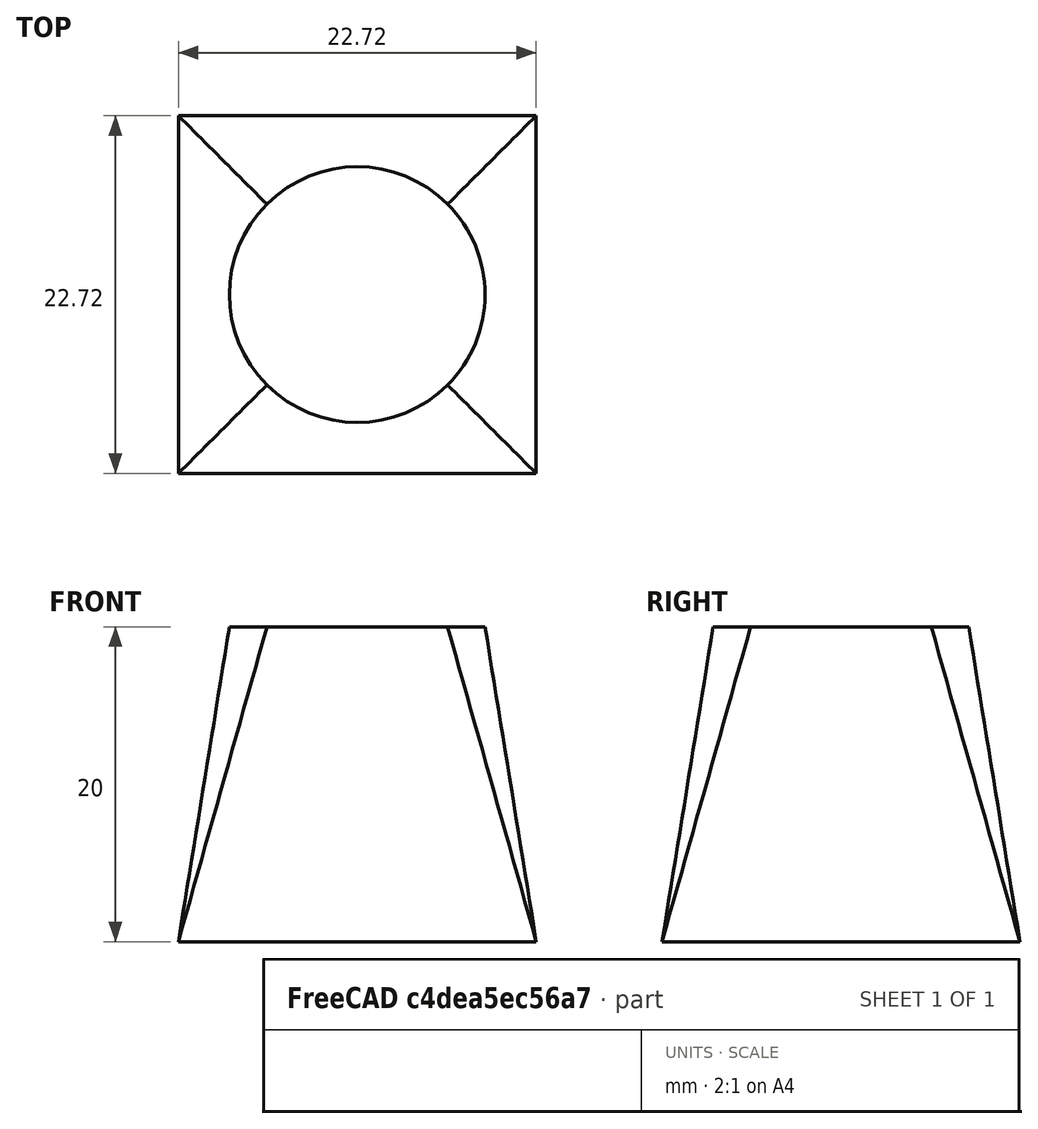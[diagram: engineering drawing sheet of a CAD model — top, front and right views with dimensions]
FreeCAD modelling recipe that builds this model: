
FCSTD DOCUMENT  (FreeCAD 0.17R13217 (Git))
Label: 15-interpolacion-secciones
License: All rights reserved
LicenseURL: http://en.wikipedia.org/wiki/All_rights_reserved
objects: Sketcher::SketchObject×2, PartDesign::AdditiveLoft×1, PartDesign::Body×1
note: 5 computed .brp shape members not serialized (recipe doc carries the construction recipe); baked Part::Feature solids carry a one-line shape summary decoded from their .brp

FEATURE [Sketcher::SketchObject] Sketch
  MapMode = 5
  Support = -> [XY_Plane]
  sketch-geometry (4):
    g0: LineSegment StartX=-11.3647 StartY=11.3647 StartZ=0 EndX=11.3647 EndY=11.3647 EndZ=0
    g1: LineSegment StartX=11.3647 StartY=11.3647 StartZ=0 EndX=11.3647 EndY=-11.3647 EndZ=0
    g2: LineSegment StartX=11.3647 StartY=-11.3647 StartZ=0 EndX=-11.3647 EndY=-11.3647 EndZ=0
    g3: LineSegment StartX=-11.3647 StartY=-11.3647 StartZ=0 EndX=-11.3647 EndY=11.3647 EndZ=0
  constraints (10):
    c: Coincident(g0,g1)
    c: Coincident(g1,g2)
    c: Coincident(g2,g3)
    c: Coincident(g3,g0)
    c: Horizontal(g0)
    c: Horizontal(g2)
    c: Vertical(g1)
    c: Vertical(g3)
    c: Equal(g2,g1)
    c: Symmetric(g0,g1,g-1)
FEATURE [Sketcher::SketchObject] Sketch001
  AttachmentOffset = pos=(0,0,20) rot=(0,0,1;0rad)
  MapMode = 5
  Placement = pos=(0,0,20) rot=(0,0,1;0rad)
  Support = -> [XY_Plane]
  sketch-geometry (1):
    g0: Circle CenterX=0 CenterY=0 CenterZ=0 NormalX=0 NormalY=0 NormalZ=1 AngleXU=0 Radius=8.11817
  constraints (1):
    c: Coincident(g0,g-1)
FEATURE [PartDesign::AdditiveLoft] AdditiveLoft
  Closed = false
  Profile = -> Sketch
  Refine = true
  Ruled = false
  Sections = -> [Sketch001]
FEATURE [PartDesign::Body] Body
  Group = -> [Sketch,Sketch001,AdditiveLoft]
  Origin = -> Origin
  Tip = -> AdditiveLoft
